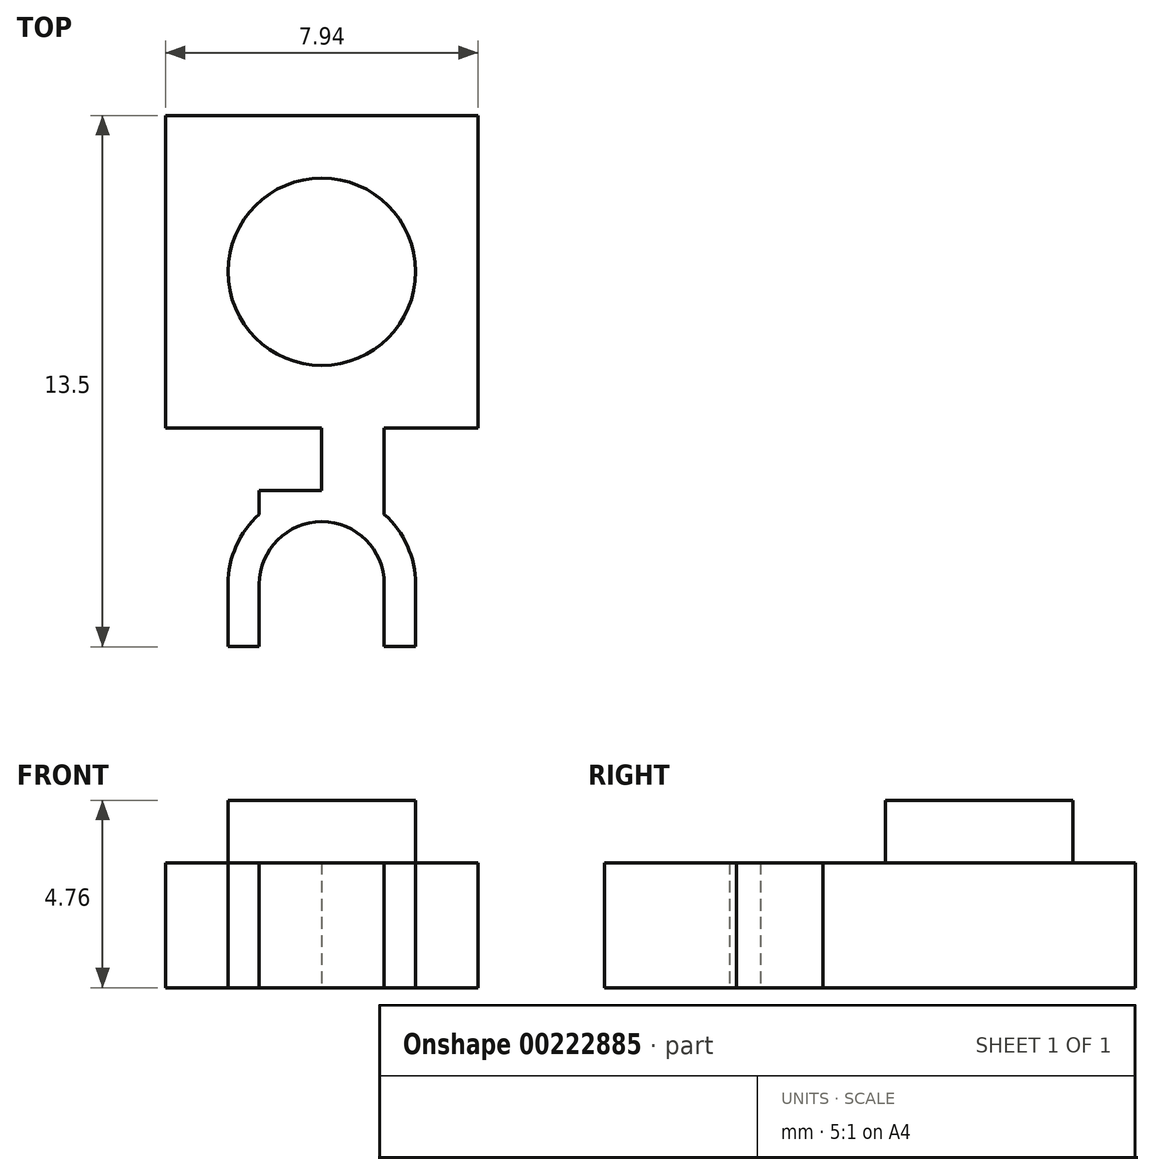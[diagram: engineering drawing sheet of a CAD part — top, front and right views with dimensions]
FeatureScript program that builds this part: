
annotation { "Feature Type Name" : "Feature", "Feature Type Description" : "" }
export const myFeature = defineFeature(function(context is Context, id is Id, definition is map)
    precondition{}
    {
        {
            var Q0;
            Q0=qCreatedBy(makeId("Top.planeOp"),FACE);
            var sketch = newSketch(context, id + "F0", { "sketchPlane" : qUnion([Q0])});
            skLineSegment(sketch, "E0.bottom", {"start": v(-3.97, 3.97) * mm, "end": v(3.97, 3.97) * mm});
            skLineSegment(sketch, "E0.top", {"start": v(-3.97, -3.97) * mm, "end": v(3.97, -3.97) * mm});
            skLineSegment(sketch, "E0.left", {"start": v(-3.97, 3.97) * mm, "end": v(-3.97, -3.97) * mm});
            skLineSegment(sketch, "E0.right", {"start": v(3.97, 3.97) * mm, "end": v(3.97, -3.97) * mm});
            skPoint(sketch, "E0.middle", {"position": v(0, 0) * mm});
            skCircle(sketch, "E1", {"center": v(0, 0) * mm, "radius": 2.38 * mm});
            skLineSegment(sketch, "E2", {"start": v(0, -3.97) * mm, "end": v(0, -5.56) * mm});
            skLineSegment(sketch, "E3.bottom", {"start": v(0, -3.97) * mm, "end": v(-1.59, -3.97) * mm});
            skLineSegment(sketch, "E3.top", {"start": v(0, -5.56) * mm, "end": v(-1.59, -5.56) * mm});
            skLineSegment(sketch, "E3.right", {"start": v(-1.59, -3.97) * mm, "end": v(-1.59, -5.56) * mm});
            skLineSegment(sketch, "E4.MirrorCS", {"start": v(0, -3.97) * mm, "end": v(1.59, -3.97) * mm});
            skLineSegment(sketch, "E5.MirrorCS", {"start": v(1.59, -3.97) * mm, "end": v(1.59, -5.56) * mm});
            skLineSegment(sketch, "E6.MirrorCS", {"start": v(0, -5.56) * mm, "end": v(1.59, -5.56) * mm});
            skLineSegment(sketch, "E7", {"start": v(-0.8, -3.97) * mm, "end": v(0.8, -3.97) * mm});
            skLineSegment(sketch, "E8", {"start": v(0, -5.56) * mm, "end": v(0, -7.94) * mm});
            skArc(sketch, "E9", {"start": v(0, -5.56) * mm, "mid": v(1.68, -6.25) * mm, "end": v(2.38, -7.94) * mm});
            skArc(sketch, "E10", {"start": v(0, -5.56) * mm, "mid": v(-1.68, -6.25) * mm, "end": v(-2.38, -7.94) * mm});
            skLineSegment(sketch, "E11", {"start": v(-1.59, -5.56) * mm, "end": v(-1.59, -6.16) * mm});
            skLineSegment(sketch, "E12", {"start": v(1.59, -5.56) * mm, "end": v(1.59, -6.16) * mm});
            skLineSegment(sketch, "E13", {"start": v(-2.38, -7.94) * mm, "end": v(-1.59, -7.94) * mm});
            skLineSegment(sketch, "E14.MirrorCS", {"start": v(2.38, -7.94) * mm, "end": v(1.59, -7.94) * mm});
            skArc(sketch, "E15", {"start": v(-1.59, -7.94) * mm, "mid": v(0, -6.35) * mm, "end": v(1.59, -7.94) * mm});
            skLineSegment(sketch, "E16.top", {"start": v(-2.38, -9.53) * mm, "end": v(-1.59, -9.53) * mm});
            skLineSegment(sketch, "E16.left", {"start": v(-2.38, -7.94) * mm, "end": v(-2.38, -9.53) * mm});
            skLineSegment(sketch, "E16.right", {"start": v(-1.59, -7.94) * mm, "end": v(-1.59, -9.53) * mm});
            skLineSegment(sketch, "E17.MirrorCS", {"start": v(1.59, -7.94) * mm, "end": v(1.59, -9.53) * mm});
            skLineSegment(sketch, "E18.MirrorCS", {"start": v(2.38, -7.94) * mm, "end": v(2.38, -9.53) * mm});
            skLineSegment(sketch, "E19.MirrorCS", {"start": v(2.38, -9.53) * mm, "end": v(1.59, -9.53) * mm});
            skSolve(sketch);
        }
        {
            var Q0;
            Q0=makeQuery(id+"F0.imprint","IMPRINT",FACE,{"disambiguationData":[TD([[makeQuery(id+"F0.imprint","IMPRINT",EDGE,{"derivedFrom":sQuery(id+"F0.wireOp",EDGE,"E0.bottom")}),-1.0]])]});
            var Q1;
            {var subQ1=sQuery(id+"F0.wireOp",EDGE,"E3.bottom");Q1=makeQuery(id+"F0.imprint","IMPRINT",FACE,{"disambiguationData":[TD([[makeQuery(id+"F0.imprint","IMPRINT",EDGE,{"derivedFrom":subQ1}),1.0]])]});}
            var Q2;
            {var subQ1=sQuery(id+"F0.wireOp",EDGE,"E2");Q2=makeQuery(id+"F0.imprint","IMPRINT",FACE,{"disambiguationData":[TD([[makeQuery(id+"F0.imprint","IMPRINT",EDGE,{"derivedFrom":subQ1}),1.0]])]});}
            var Q3;
            {var subQ0=sQuery(id+"F0.wireOp",EDGE,"E6.MirrorCS");Q3=makeQuery(id+"F0.imprint","IMPRINT",FACE,{"disambiguationData":[TD([[makeQuery(id+"F0.imprint","IMPRINT",EDGE,{"derivedFrom":subQ0}),-1.0]])]});}
            var Q4;
            {var subQ0=sQuery(id+"F0.wireOp",EDGE,"E3.top");Q4=makeQuery(id+"F0.imprint","IMPRINT",FACE,{"disambiguationData":[TD([[makeQuery(id+"F0.imprint","IMPRINT",EDGE,{"derivedFrom":subQ0}),1.0]])]});}
            var Q5;
            {var subQ0=sQuery(id+"F0.wireOp",EDGE,"E13");Q5=makeQuery(id+"F0.imprint","IMPRINT",FACE,{"disambiguationData":[TD([[makeQuery(id+"F0.imprint","IMPRINT",EDGE,{"derivedFrom":subQ0}),1.0]])]});}
            var Q6;
            Q6=makeQuery(id+"F0.imprint","IMPRINT",FACE,{"disambiguationData":[TD([[makeQuery(id+"F0.imprint","IMPRINT",EDGE,{"derivedFrom":sQuery(id+"F0.wireOp",EDGE,"E13")}),-1.0]])]});
            var Q7;
            {var subQ0=sQuery(id+"F0.wireOp",EDGE,"E14.MirrorCS");Q7=makeQuery(id+"F0.imprint","IMPRINT",FACE,{"disambiguationData":[TD([[makeQuery(id+"F0.imprint","IMPRINT",EDGE,{"derivedFrom":subQ0}),-1.0]])]});}
            var Q8;
            Q8=makeQuery(id+"F0.imprint","IMPRINT",FACE,{"disambiguationData":[TD([[makeQuery(id+"F0.imprint","IMPRINT",EDGE,{"derivedFrom":sQuery(id+"F0.wireOp",EDGE,"E17.MirrorCS")}),1.0]])]});
            extrude(context, id + "F1", {"entities" : qUnion([Q0, Q1, Q2, Q3, Q4, Q5, Q6, Q7, Q8]), "depth" : 3.17 * mm});
        }
        {
            var Q0;
            Q0=makeQuery(id+"F0.imprint","IMPRINT",FACE,{"disambiguationData":[TD([[makeQuery(id+"F0.imprint","IMPRINT",EDGE,{"derivedFrom":sQuery(id+"F0.wireOp",EDGE,"E1")}),1.0]])]});
            extrude(context, id + "F2", {"entities" : qUnion([Q0]), "operationType" : NewBodyOperationType.ADD, "depth" : 4.76 * mm});
        }
    });
